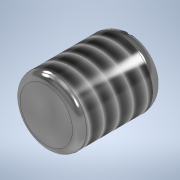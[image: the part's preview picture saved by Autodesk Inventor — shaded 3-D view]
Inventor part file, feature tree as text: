
AUTODESK INVENTOR PART (.ipt)
format: ipt  version: 2020 (Build 240168000, 168)  size: 167,424 bytes
history: native  units: in
note: dims shown in document units (in); Inventor stores cm internally (conversion verified against a paired STEP export)
features: extrude x2, fillet x2, sketch x2, thread x1
ambient origin geometry x8: Origin, YZ Plane, XZ Plane, XY Plane, X Axis, Y Axis, Z Axis, Center Point
bodies: Solid1 (feature_tree)
feature tree (7):
  extrude  "Extrusion1"  Depth=0.25in TaperAngle=0.0deg
  thread  "Thread1"  [1 undecoded]
  fillet  "Fillet1"  Radius=0.02in
  fillet  "Fillet2"  Radius=0.04in
  extrude  "Extrusion2"  Depth=0.0185in
  sketch  "Sketch1"  dims[d0=0.19in d1=0.25in d2=0.0in d3=0.25in d4=0.0in d5=0.02in d6=0.04in]
  sketch  "Sketch2"  dims[d7=0.2in d8=0.0185in d9=0.03in d10=0.0in]
note: 1 required parameter value undecoded (feature->parameter linkage not recoverable at this tier; creation-order binding heuristic only, values carry confidence <= 0.55)
